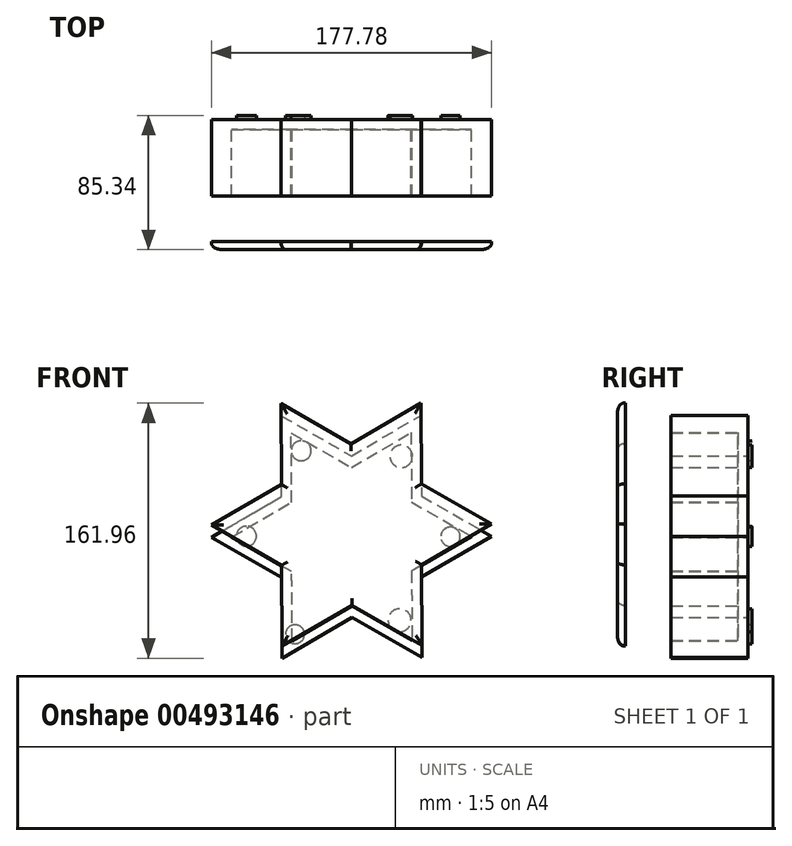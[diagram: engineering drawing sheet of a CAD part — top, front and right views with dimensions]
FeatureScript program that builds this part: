
annotation { "Feature Type Name" : "Feature", "Feature Type Description" : "" }
export const myFeature = defineFeature(function(context is Context, id is Id, definition is map)
    precondition{}
    {
        {
            var Q0;
            Q0=qCreatedBy(makeId("Front.planeOp"),FACE);
            var sketch = newSketch(context, id + "F0", { "sketchPlane" : qUnion([Q0])});
            skCircle(sketch, "E0.cCircle", {"center": v(0, 0) * mm, "radius": 44.44 * mm, "construction": true});
            skLineSegment(sketch, "E0.0", {"start": v(88.88, 0.33) * mm, "end": v(-44.15, -77.13) * mm});
            skLineSegment(sketch, "E0.1", {"start": v(-44.15, -77.13) * mm, "end": v(-44.72, 76.8) * mm});
            skLineSegment(sketch, "E0.2", {"start": v(-44.72, 76.8) * mm, "end": v(88.88, 0.33) * mm});
            skPoint(sketch, "E0.0.midPoint", {"position": v(22.36, -38.4) * mm});
            skLineSegment(sketch, "E1.0", {"start": v(44.72, -76.8) * mm, "end": v(-88.88, -0.33) * mm});
            skLineSegment(sketch, "E1.1", {"start": v(-88.88, -0.33) * mm, "end": v(44.15, 77.13) * mm});
            skLineSegment(sketch, "E1.2", {"start": v(44.15, 77.13) * mm, "end": v(44.72, -76.8) * mm});
            skPoint(sketch, "E1.0.midPoint", {"position": v(-22.08, -38.57) * mm});
            skSolve(sketch);
        }
        {
            var Q0;
            {var subQ1=sQuery(id+"F0.wireOp",EDGE,"E0.0");var subQ8=sQuery(id+"F0.wireOp",EDGE,"E1.2");var subQ11=makeQuery(id+"F0.imprint","INTERSECT",VERTEX,{"derivedFrom":[subQ1,subQ8]});Q0=makeQuery(id+"F0.imprint","IMPRINT",FACE,{"disambiguationData":[TD([[makeQuery(id+"F0.imprint","IMPRINT",EDGE,{"disambiguationData":[TD([[subQ11,-1.0]])],"derivedFrom":subQ1}),-1.0]])]});}
            var Q1;
            {var subQ0=sQuery(id+"F0.wireOp",EDGE,"E1.1");var subQ1=sQuery(id+"F0.wireOp",EDGE,"E0.2");var subQ2=makeQuery(id+"F0.imprint","INTERSECT",VERTEX,{"derivedFrom":[subQ1,subQ0]});Q1=makeQuery(id+"F0.imprint","IMPRINT",FACE,{"disambiguationData":[TD([[makeQuery(id+"F0.imprint","IMPRINT",EDGE,{"disambiguationData":[TD([[subQ2,-1.0]])],"derivedFrom":subQ1}),1.0]])]});}
            var Q2;
            {var subQ0=sQuery(id+"F0.wireOp",EDGE,"E0.2");var subQ1=sQuery(id+"F0.wireOp",EDGE,"E0.0");var subQ2=makeQuery(id+"F0.imprint","INTERSECT",VERTEX,{"derivedFrom":[subQ1,subQ0]});Q2=makeQuery(id+"F0.imprint","IMPRINT",FACE,{"disambiguationData":[TD([[makeQuery(id+"F0.imprint","IMPRINT",EDGE,{"disambiguationData":[TD([[subQ2,-1.0]])],"derivedFrom":subQ1}),-1.0]])]});}
            var Q3;
            {var subQ0=sQuery(id+"F0.wireOp",EDGE,"E1.2");var subQ1=sQuery(id+"F0.wireOp",EDGE,"E0.0");var subQ2=makeQuery(id+"F0.imprint","INTERSECT",VERTEX,{"derivedFrom":[subQ1,subQ0]});Q3=makeQuery(id+"F0.imprint","IMPRINT",FACE,{"disambiguationData":[TD([[makeQuery(id+"F0.imprint","IMPRINT",EDGE,{"disambiguationData":[TD([[subQ2,-1.0]])],"derivedFrom":subQ1}),1.0]])]});}
            var Q4;
            {var subQ0=sQuery(id+"F0.wireOp",EDGE,"E0.1");var subQ1=sQuery(id+"F0.wireOp",EDGE,"E0.0");var subQ2=makeQuery(id+"F0.imprint","INTERSECT",VERTEX,{"derivedFrom":[subQ1,subQ0]});Q4=makeQuery(id+"F0.imprint","IMPRINT",FACE,{"disambiguationData":[TD([[makeQuery(id+"F0.imprint","IMPRINT",EDGE,{"disambiguationData":[TD([[subQ2,1.0]])],"derivedFrom":subQ1}),-1.0]])]});}
            var Q5;
            {var subQ0=sQuery(id+"F0.wireOp",EDGE,"E1.0");var subQ1=sQuery(id+"F0.wireOp",EDGE,"E0.1");var subQ2=makeQuery(id+"F0.imprint","INTERSECT",VERTEX,{"derivedFrom":[subQ1,subQ0]});Q5=makeQuery(id+"F0.imprint","IMPRINT",FACE,{"disambiguationData":[TD([[makeQuery(id+"F0.imprint","IMPRINT",EDGE,{"disambiguationData":[TD([[subQ2,-1.0]])],"derivedFrom":subQ1}),1.0]])]});}
            var Q6;
            {var subQ0=sQuery(id+"F0.wireOp",EDGE,"E0.2");var subQ1=sQuery(id+"F0.wireOp",EDGE,"E0.1");var subQ2=makeQuery(id+"F0.imprint","INTERSECT",VERTEX,{"derivedFrom":[subQ1,subQ0]});Q6=makeQuery(id+"F0.imprint","IMPRINT",FACE,{"disambiguationData":[TD([[makeQuery(id+"F0.imprint","IMPRINT",EDGE,{"disambiguationData":[TD([[subQ2,1.0]])],"derivedFrom":subQ1}),-1.0]])]});}
            extrude(context, id + "F1", {"entities" : qUnion([Q0, Q1, Q2, Q3, Q4, Q5, Q6]), "depth" : 48.77 * mm});
        }
        {
            var Q0;
            Q0=makeQuery(id+"F1.opExtrude","CAP_FACE",FACE,{"disambiguationData":[OSD([sQuery(id+"F0.wireOp",EDGE,"E0.0"),sQuery(id+"F0.wireOp",EDGE,"E0.1"),sQuery(id+"F0.wireOp",EDGE,"E0.2"),sQuery(id+"F0.wireOp",EDGE,"E1.0"),sQuery(id+"F0.wireOp",EDGE,"E1.1"),sQuery(id+"F0.wireOp",EDGE,"E1.2")])],"isStart":false});
            shell(context, id + "F2", {"entities" : qUnion([Q0]), "thickness" : 6.35 * mm});
        }
        {
            var Q0;
            Q0=makeQuery(id+"F2.opShell","OFFSET_FACE",FACE,{"disambiguationData":[OSD([sQuery(id+"F0.wireOp",EDGE,"E0.0"),sQuery(id+"F0.wireOp",EDGE,"E0.1"),sQuery(id+"F0.wireOp",EDGE,"E0.2"),sQuery(id+"F0.wireOp",EDGE,"E1.0"),sQuery(id+"F0.wireOp",EDGE,"E1.1"),sQuery(id+"F0.wireOp",EDGE,"E1.2")])]});
            cPlane(context, id + "F3", {"entities" : qUnion([Q0]), "cplaneType" : CPlaneType.OFFSET, "offset" : 71.37 * mm, "width" : 152.4 * mm, "height" : 152.4 * mm});
        }
        {
            var Q0;
            Q0=qCreatedBy(id+"F3.planeOp",FACE);
            var sketch = newSketch(context, id + "F4", { "sketchPlane" : qUnion([Q0])});
            skCircle(sketch, "E2.cCircle", {"center": v(-0.03, 7.7) * mm, "radius": 44.44 * mm, "construction": true});
            skLineSegment(sketch, "E2.0", {"start": v(88.85, 8.03) * mm, "end": v(-44.18, -69.44) * mm});
            skLineSegment(sketch, "E2.1", {"start": v(-44.18, -69.44) * mm, "end": v(-44.75, 84.5) * mm});
            skLineSegment(sketch, "E2.2", {"start": v(-44.75, 84.5) * mm, "end": v(88.85, 8.03) * mm});
            skPoint(sketch, "E2.0.midPoint", {"position": v(22.33, -30.7) * mm});
            skLineSegment(sketch, "E3.0", {"start": v(44.7, -69.1) * mm, "end": v(-88.9, 7.37) * mm});
            skLineSegment(sketch, "E3.1", {"start": v(-88.9, 7.37) * mm, "end": v(44.12, 84.83) * mm});
            skLineSegment(sketch, "E3.2", {"start": v(44.12, 84.83) * mm, "end": v(44.7, -69.1) * mm});
            skPoint(sketch, "E3.0.midPoint", {"position": v(-22.1, -30.87) * mm});
            skSolve(sketch);
        }
        {
            var Q0;
            Q0 = qSketchRegion(id + "F4", true);
            extrude(context, id + "F5", {"entities" : qUnion([Q0]), "depth" : 5.08 * mm, "offsetDistance" : 25.4 * mm});
        }
        {
            var Q0;
            Q0=makeQuery(id+"F5.opExtrude","CAP_FACE",FACE,{"disambiguationData":[OSD([sQuery(id+"F4.wireOp",EDGE,"E2.0"),sQuery(id+"F4.wireOp",EDGE,"E2.1"),sQuery(id+"F4.wireOp",EDGE,"E2.2"),sQuery(id+"F4.wireOp",EDGE,"E3.0"),sQuery(id+"F4.wireOp",EDGE,"E3.1"),sQuery(id+"F4.wireOp",EDGE,"E3.2")])],"isStart":false});
            fillet(context, id + "F6", {"entities" : qUnion([Q0]), "radius" : 3.8 * mm, "tangentPropagation" : true, "allowEdgeOverflow" : false});
        }
        {
            var Q0;
            Q0=makeQuery(id+"F1.opExtrude","CAP_FACE",FACE,{"disambiguationData":[OSD([sQuery(id+"F0.wireOp",EDGE,"E0.0"),sQuery(id+"F0.wireOp",EDGE,"E0.1"),sQuery(id+"F0.wireOp",EDGE,"E0.2"),sQuery(id+"F0.wireOp",EDGE,"E1.0"),sQuery(id+"F0.wireOp",EDGE,"E1.1"),sQuery(id+"F0.wireOp",EDGE,"E1.2")])],"isStart":true});
            var sketch = newSketch(context, id + "F7", { "sketchPlane" : qUnion([Q0])});
            skCircle(sketch, "E4", {"center": v(-31.55, 51.05) * mm, "radius": 7.15 * mm});
            skCircle(sketch, "E5", {"center": v(-62.82, 0) * mm, "radius": 6.17 * mm});
            skCircle(sketch, "E6", {"center": v(-30.55, -53.06) * mm, "radius": 7.3 * mm});
            skCircle(sketch, "E7", {"center": v(31.97, 54.6) * mm, "radius": 6.34 * mm});
            skCircle(sketch, "E8", {"center": v(66.75, 0.33) * mm, "radius": 6.35 * mm});
            skCircle(sketch, "E9", {"center": v(35.92, -61.93) * mm, "radius": 6 * mm});
            skSolve(sketch);
        }
        {
            var Q0;
            Q0 = qSketchRegion(id + "F7", true);
            extrude(context, id + "F8", {"entities" : qUnion([Q0]), "operationType" : NewBodyOperationType.ADD, "depth" : 2.54 * mm, "offsetDistance" : 25.4 * mm});
        }
    });
